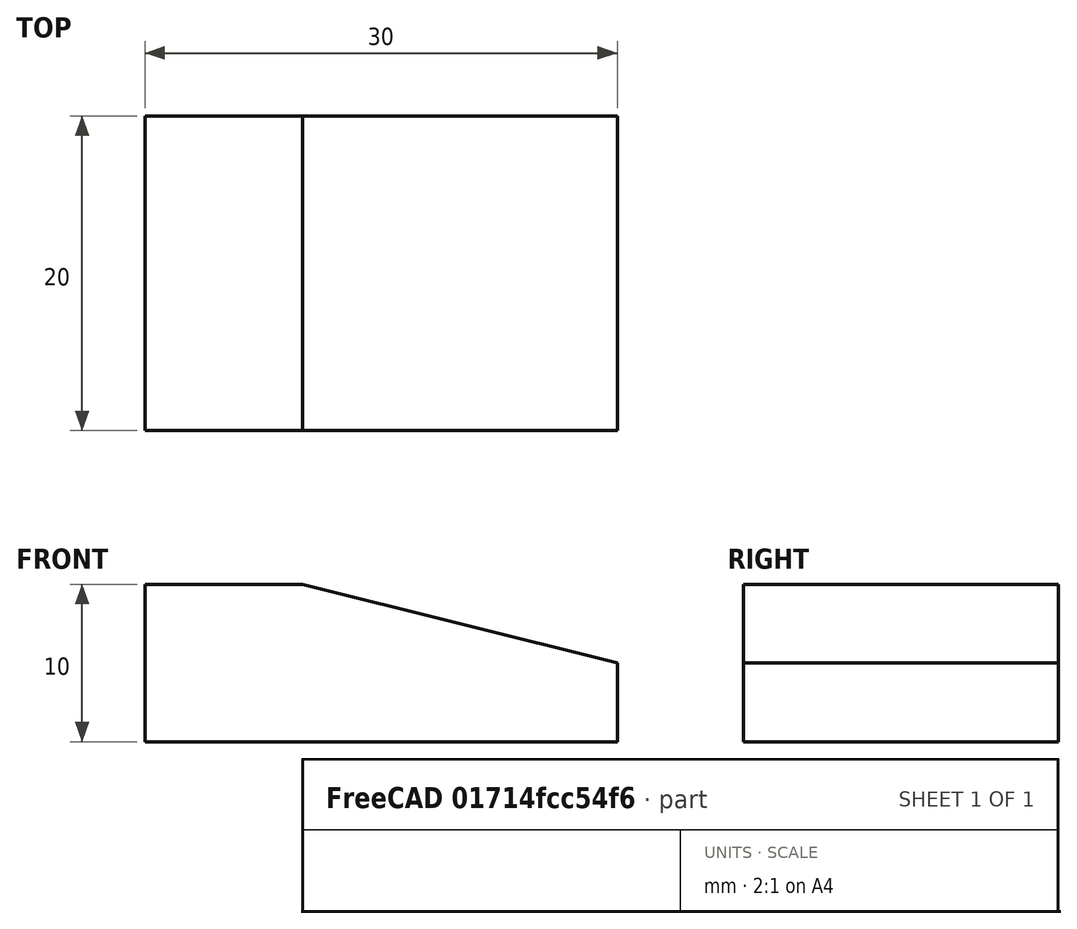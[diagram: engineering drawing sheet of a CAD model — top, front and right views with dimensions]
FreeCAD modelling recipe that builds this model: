
FCSTD DOCUMENT  (FreeCAD 0.19R)
Label: gp1
License: All rights reserved
LicenseURL: http://en.wikipedia.org/wiki/All_rights_reserved
objects: Sketcher::SketchObject×1, PartDesign::Pad×1, PartDesign::Body×1, Mesh::Feature×1
note: 4 computed .brp shape members not serialized (recipe doc carries the construction recipe); baked Part::Feature solids carry a one-line shape summary decoded from their .brp

FEATURE [Sketcher::SketchObject] Sketch
  FullyConstrained = true
  MapMode = 5
  Placement = pos=(0,0,0) rot=(1,0,0;1.5708rad)
  Support = -> [XZ_Plane]
  sketch-geometry (6):
    g0: LineSegment StartX=0 StartY=0 StartZ=0 EndX=0 EndY=10 EndZ=0
    g1: LineSegment StartX=0 StartY=10 StartZ=0 EndX=10 EndY=10 EndZ=0
    g2: LineSegment StartX=10 StartY=10 StartZ=0 EndX=30 EndY=5 EndZ=0
    g3: LineSegment StartX=30 StartY=5 StartZ=0 EndX=30 EndY=0 EndZ=0
    g4: LineSegment StartX=30 StartY=0 StartZ=0 EndX=0 EndY=0 EndZ=0
    g5: GeomPoint X=1e-16 Y=5 Z=0
  constraints (15):
    c: Coincident(g0,g-1)
    c: Vertical(g0)
    c: Coincident(g1,g0)
    c: Horizontal(g1)
    c: Coincident(g2,g1)
    c: Coincident(g3,g2)
    c: PointOnObject(g3,g-1)
    c: Vertical(g3)
    c: Coincident(g4,g3)
    c: Coincident(g4,g0)
    c: DistanceX(g4,g4) = 30
    c: Symmetric(g0,g0,g5)
    c: Horizontal(g5,g2)
    c: DistanceY(g0,g0) = 10
    c: Equal(g1,g0)
FEATURE [PartDesign::Pad] Pad
  Direction = (1,1,1)
  Length = 20
  Length2 = 100
  Midplane = true
  Placement = pos=(0,0,0) rot=(1,0,0;1.5708rad)
  Profile = -> Sketch
  Type = 0
FEATURE [PartDesign::Body] Body
  Group = -> [Sketch,Pad]
  Origin = -> Origin
  Tip = -> Pad
FEATURE [Mesh::Feature] Mesh  label="Body (Meshed)"
